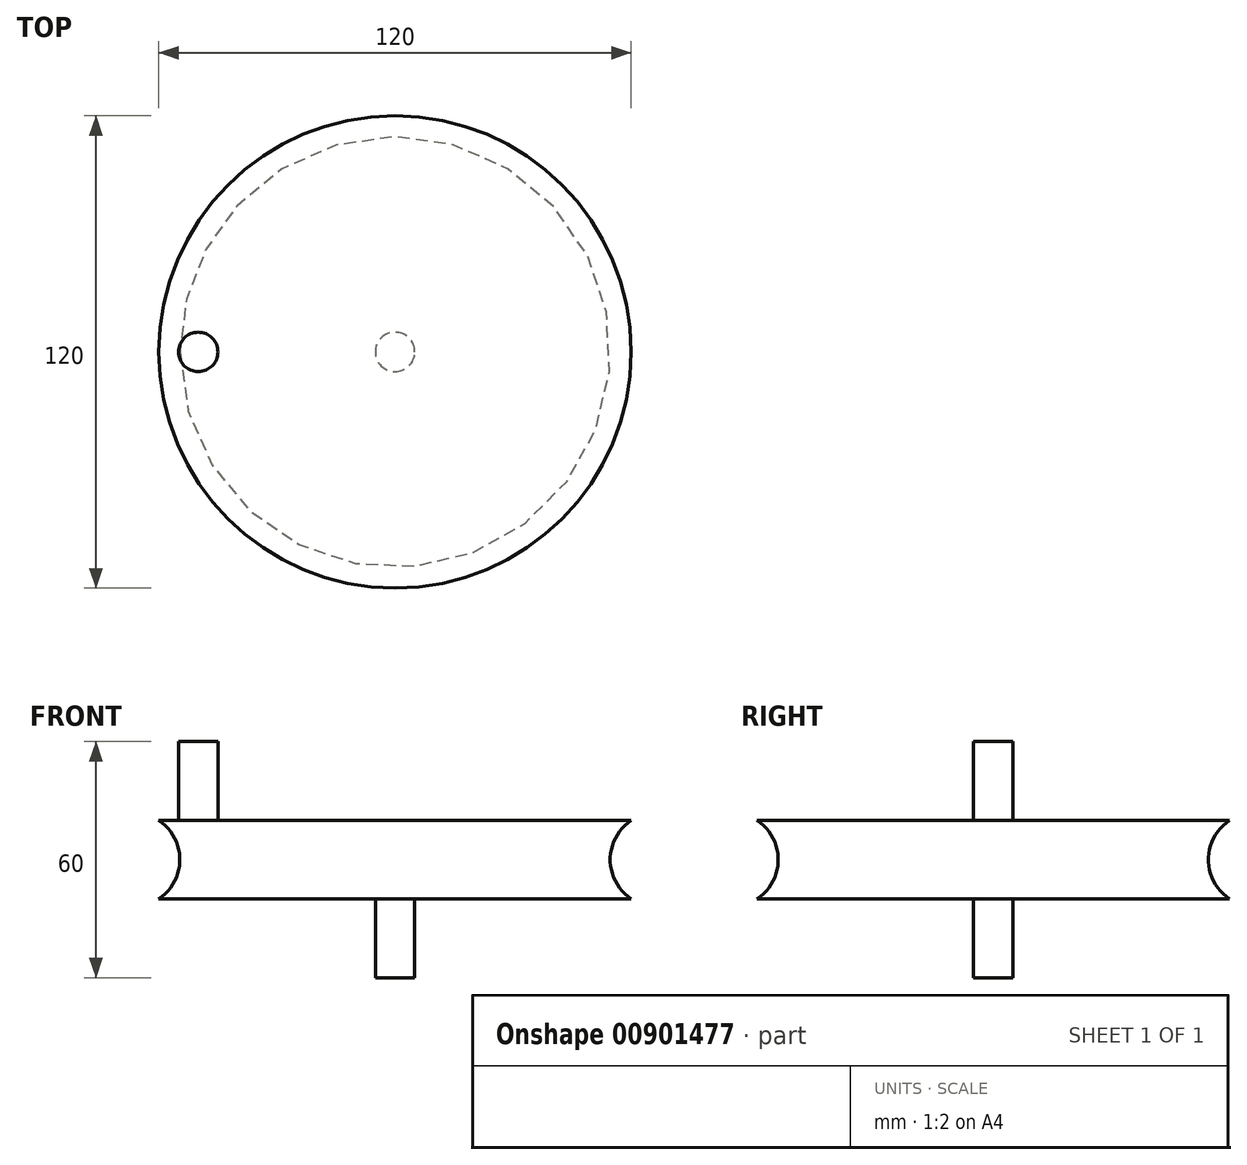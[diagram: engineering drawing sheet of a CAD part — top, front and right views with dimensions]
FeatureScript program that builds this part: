
annotation { "Feature Type Name" : "Feature", "Feature Type Description" : "" }
export const myFeature = defineFeature(function(context is Context, id is Id, definition is map)
    precondition{}
    {
        {
            var Q0;
            Q0=qCreatedBy(makeId("Front.planeOp"),FACE);
            var sketch = newSketch(context, id + "F0", { "sketchPlane" : qUnion([Q0])});
            skLineSegment(sketch, "E0", {"start": v(0, 0) * mm, "end": v(0, 70) * mm});
            skLineSegment(sketch, "E1", {"start": v(0, 70) * mm, "end": v(5, 70) * mm});
            skLineSegment(sketch, "E2", {"start": v(5, 70) * mm, "end": v(5, 40) * mm});
            skLineSegment(sketch, "E3", {"start": v(5, 40) * mm, "end": v(60, 40) * mm});
            skLineSegment(sketch, "E4", {"start": v(60, 40) * mm, "end": v(60, 20) * mm});
            skLineSegment(sketch, "E5", {"start": v(60, 20) * mm, "end": v(5, 20) * mm});
            skLineSegment(sketch, "E6", {"start": v(5, 20) * mm, "end": v(5, 0) * mm});
            skLineSegment(sketch, "E7", {"start": v(5, 0) * mm, "end": v(0, 0) * mm});
            skArc(sketch, "E8", {"start": v(60, 40) * mm, "mid": v(54.66, 30) * mm, "end": v(60, 20) * mm});
            skSolve(sketch);
        }
        {
            var Q0;
            Q0=makeQuery(id+"F0.imprint","IMPRINT",FACE,{"disambiguationData":[TD([[makeQuery(id+"F0.imprint","IMPRINT",EDGE,{"derivedFrom":sQuery(id+"F0.wireOp",EDGE,"E0")}),-1.0]])]});
            var Q1;
            Q1=sQuery(id+"F0.wireOp",EDGE,"E0");
            revolve(context, id + "F1", {"surfaceOperationType" : NewSurfaceOperationType.NEW, "entities" : qUnion([Q0]), "axis" : qUnion([Q1]), "revolveType" : RevolveType.FULL});
        }
        {
            var Q0;
            Q0=makeQuery(id+"F1.opRevolve","SWEPT_FACE",FACE,{"disambiguationData":[OSD([sQuery(id+"F0.wireOp",EDGE,"E3")])]});
            var sketch = newSketch(context, id + "F2", { "sketchPlane" : qUnion([Q0])});
            skCircle(sketch, "E9", {"center": v(-50, 0) * mm, "radius": 5 * mm});
            skSolve(sketch);
        }
        {
            var Q0;
            Q0 = qSketchRegion(id + "F2", true);
            extrude(context, id + "F3", {"entities" : qUnion([Q0]), "operationType" : NewBodyOperationType.ADD, "depth" : 20 * mm, "offsetDistance" : 25 * mm});
        }
        {
            var Q0;
            Q0=makeQuery(id+"F1.opRevolve","SWEPT_FACE",FACE,{"disambiguationData":[OSD([sQuery(id+"F0.wireOp",EDGE,"E1")])]});
            var sketch = newSketch(context, id + "F4", { "sketchPlane" : qUnion([Q0])});
            skCircle(sketch, "E10.0", {"center": v(0, 0) * mm, "radius": 5 * mm});
            skSolve(sketch);
        }
        {
            var Q0;
            Q0 = qSketchRegion(id + "F4", true);
            extrude(context, id + "F5", {"entities" : qUnion([Q0]), "operationType" : NewBodyOperationType.REMOVE, "oppositeDirection" : true, "depth" : 30 * mm, "offsetDistance" : 25 * mm});
        }
    });
